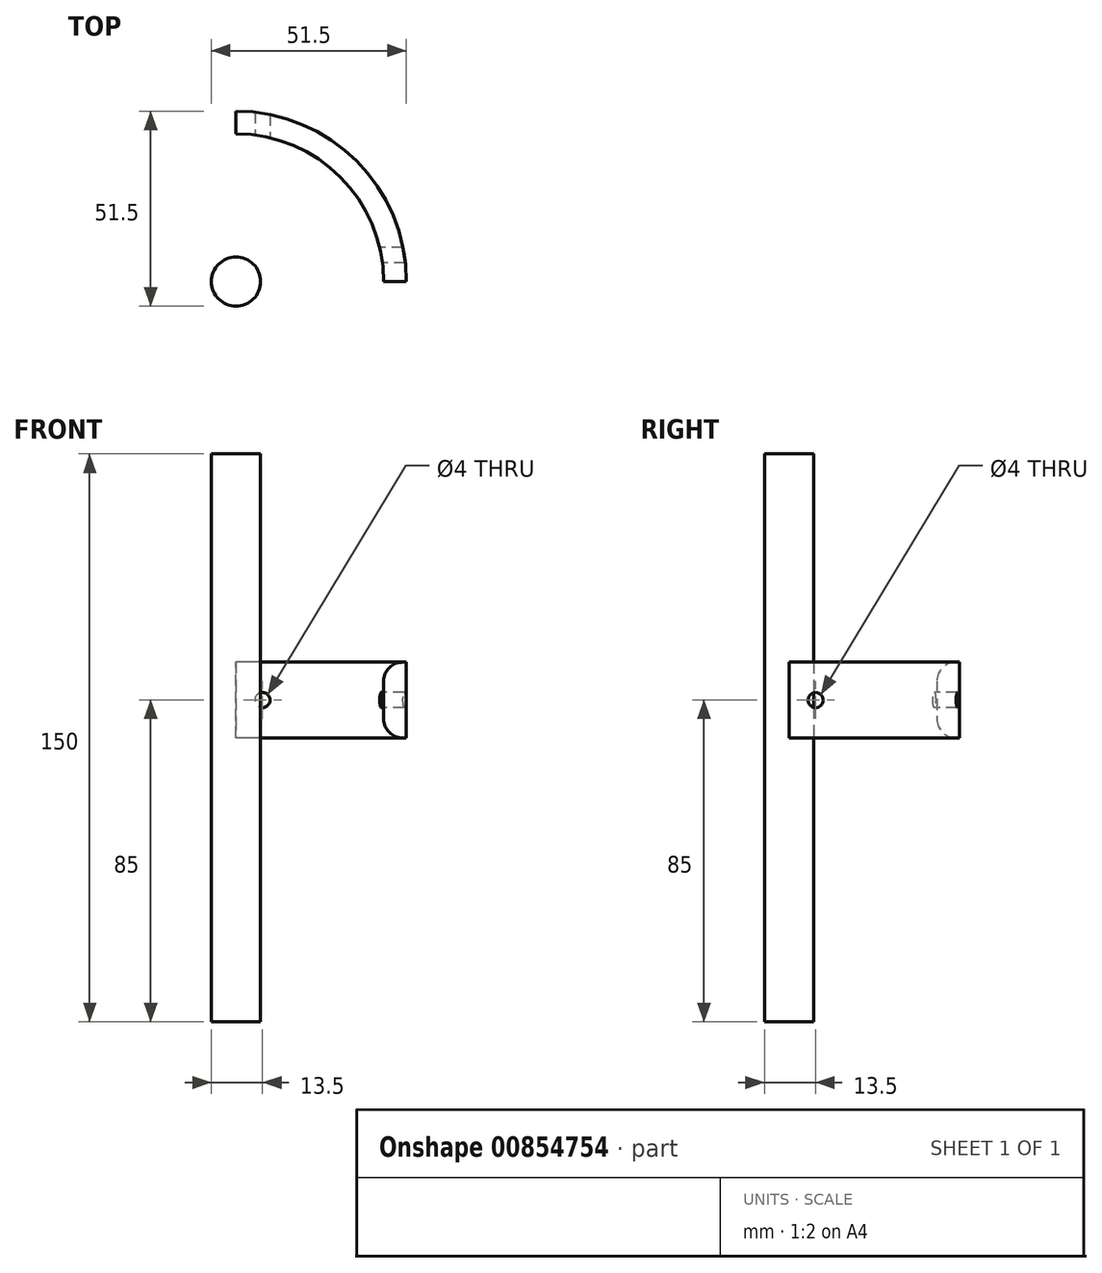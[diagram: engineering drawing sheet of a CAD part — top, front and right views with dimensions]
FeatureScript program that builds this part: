
annotation { "Feature Type Name" : "Feature", "Feature Type Description" : "" }
export const myFeature = defineFeature(function(context is Context, id is Id, definition is map)
    precondition{}
    {
        {
            var Q0;
            Q0=qCreatedBy(makeId("Top.planeOp"),FACE);
            var sketch = newSketch(context, id + "F0", { "sketchPlane" : qUnion([Q0])});
            skCircle(sketch, "E0", {"center": v(0, 0) * mm, "radius": 45 * mm});
            skCircle(sketch, "E1.0", {"center": v(0, 0) * mm, "radius": 39 * mm});
            skSolve(sketch);
        }
        {
            var Q0;
            Q0 = qSketchRegion(id + "F0", true);
            extrude(context, id + "F1", {"entities" : qUnion([Q0]), "depth" : 20 * mm, "offsetDistance" : 25 * mm});
        }
        {
            var Q0;
            Q0=makeQuery(id+"F1.opExtrude","CAP_FACE",FACE,{"disambiguationData":[OSD([sQuery(id+"F0.wireOp",EDGE,"E0"),sQuery(id+"F0.wireOp",EDGE,"E1.0")])],"isStart":false});
            var sketch = newSketch(context, id + "F2", { "sketchPlane" : qUnion([Q0])});
            skLineSegment(sketch, "E2.bottom", {"start": v(0, 0) * mm, "end": v(45, 0) * mm});
            skLineSegment(sketch, "E2.top", {"start": v(0, 45) * mm, "end": v(45, 45) * mm});
            skLineSegment(sketch, "E2.left", {"start": v(0, 0) * mm, "end": v(0, 45) * mm});
            skLineSegment(sketch, "E2.right", {"start": v(45, 0) * mm, "end": v(45, 45) * mm});
            skSolve(sketch);
        }
        {
            var Q0;
            Q0 = qSketchRegion(id + "F2", true);
            extrude(context, id + "F3", {"entities" : qUnion([Q0]), "operationType" : NewBodyOperationType.INTERSECT, "oppositeDirection" : true, "depth" : 20 * mm, "offsetDistance" : 25 * mm});
        }
        {
            var Q0;
            Q0=qCreatedBy(makeId("Front.planeOp"),FACE);
            var sketch = newSketch(context, id + "F4", { "sketchPlane" : qUnion([Q0])});
            skCircle(sketch, "E3", {"center": v(7, 10) * mm, "radius": 2 * mm});
            skPoint(sketch, "E3.first.point", {"position": v(5.93, 11.7) * mm});
            skPoint(sketch, "E3.second.point", {"position": v(8.61, 8.82) * mm});
            skPoint(sketch, "E3.third.point", {"position": v(5.17, 9.2) * mm});
            skSolve(sketch);
        }
        {
            var Q0;
            Q0 = qSketchRegion(id + "F4", true);
            extrude(context, id + "F5", {"entities" : qUnion([Q0]), "operationType" : NewBodyOperationType.REMOVE, "oppositeDirection" : true, "depth" : 46.6 * mm, "offsetDistance" : 25 * mm});
        }
        {
            var Q0;
            Q0=qCreatedBy(makeId("Right.planeOp"),FACE);
            var sketch = newSketch(context, id + "F6", { "sketchPlane" : qUnion([Q0])});
            skCircle(sketch, "E4", {"center": v(7, 10) * mm, "radius": 2 * mm});
            skPoint(sketch, "E4.first.point", {"position": v(8.52, 11.3) * mm});
            skPoint(sketch, "E4.second.point", {"position": v(5.79, 8.41) * mm});
            skPoint(sketch, "E4.third.point", {"position": v(8.84, 9.21) * mm});
            skSolve(sketch);
        }
        {
            var Q0;
            Q0 = qSketchRegion(id + "F6", true);
            extrude(context, id + "F7", {"entities" : qUnion([Q0]), "operationType" : NewBodyOperationType.REMOVE, "depth" : 47.9 * mm, "offsetDistance" : 25 * mm});
        }
        {
            var Q0;
            Q0=makeQuery(id+"F1.opExtrude","CAP_EDGE",EDGE,{"disambiguationData":[OSD([sQuery(id+"F0.wireOp",EDGE,"E1.0")])],"isStart":false});
            var Q1;
            Q1=makeQuery(id+"F3.boolean.opBoolean","INTERSECT",EDGE,{"derivedFrom":[makeQuery(id+"F1.opExtrude","SWEPT_FACE",FACE,{"disambiguationData":[OSD([sQuery(id+"F0.wireOp",EDGE,"E1.0")])]}),makeQuery(id+"F3.boolean.toolComplement.opBoolean","COPY",FACE,{"derivedFrom":makeQuery(id+"F3.opExtrude","SWEPT_FACE",FACE,{"disambiguationData":[OSD([sQuery(id+"F2.wireOp",EDGE,"E2.bottom")])]})})]});
            var Q2;
            Q2=makeQuery(id+"F3.boolean.opBoolean","INTERSECT",EDGE,{"derivedFrom":[makeQuery(id+"F1.opExtrude","SWEPT_FACE",FACE,{"disambiguationData":[OSD([sQuery(id+"F0.wireOp",EDGE,"E1.0")])]}),makeQuery(id+"F3.boolean.toolComplement.opBoolean","COPY",FACE,{"derivedFrom":makeQuery(id+"F3.opExtrude","SWEPT_FACE",FACE,{"disambiguationData":[OSD([sQuery(id+"F2.wireOp",EDGE,"E2.left")])]})})]});
            var Q3;
            Q3=makeQuery(id+"F1.opExtrude","CAP_EDGE",EDGE,{"disambiguationData":[OSD([sQuery(id+"F0.wireOp",EDGE,"E1.0")])],"isStart":true});
            fillet(context, id + "F8", {"entities" : qUnion([Q0, Q1, Q2, Q3]), "radius" : 5 * mm, "tangentPropagation" : true, "allowEdgeOverflow" : false});
        }
        {
            var Q0;
            Q0=qCreatedBy(makeId("Top.planeOp"),FACE);
            var sketch = newSketch(context, id + "F9", { "sketchPlane" : qUnion([Q0])});
            skCircle(sketch, "E5", {"center": v(0, 0) * mm, "radius": 6.5 * mm});
            skSolve(sketch);
        }
        {
            var Q0;
            Q0 = qSketchRegion(id + "F9", true);
            extrude(context, id + "F10", {"entities" : qUnion([Q0]), "endBound" : BoundingType.SYMMETRIC, "depth" : 150 * mm, "offsetDistance" : 25 * mm});
        }
    });
